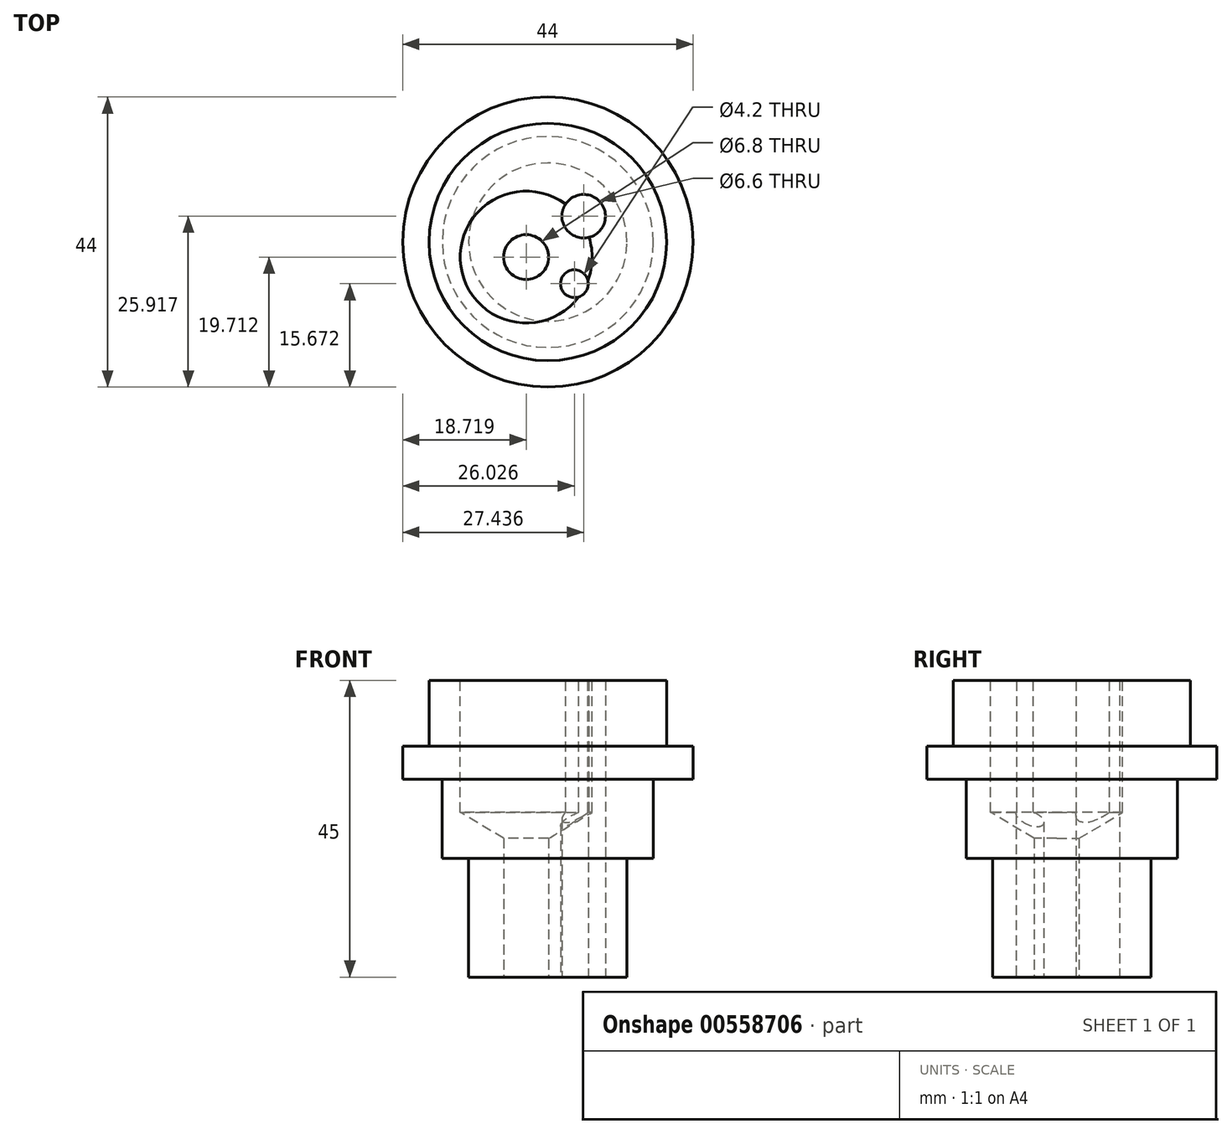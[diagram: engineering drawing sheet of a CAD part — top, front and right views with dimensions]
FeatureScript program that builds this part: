
annotation { "Feature Type Name" : "Feature", "Feature Type Description" : "" }
export const myFeature = defineFeature(function(context is Context, id is Id, definition is map)
    precondition{}
    {
        {
            var Q0;
            Q0=qCreatedBy(makeId("Top.planeOp"),FACE);
            var sketch = newSketch(context, id + "F0", { "sketchPlane" : qUnion([Q0])});
            skCircle(sketch, "E0", {"center": v(0, 0) * mm, "radius": 12 * mm});
            skCircle(sketch, "E1", {"center": v(0, 0) * mm, "radius": 18 * mm});
            skCircle(sketch, "E2", {"center": v(5.44, 3.92) * mm, "radius": 8.25 * mm, "construction": true});
            skCircle(sketch, "E3", {"center": v(5.44, 3.92) * mm, "radius": 3.3 * mm, "construction": true});
            skCircle(sketch, "E4", {"center": v(-3.28, -2.29) * mm, "radius": 4 * mm, "construction": true});
            skCircle(sketch, "E5", {"center": v(-3.28, -2.29) * mm, "radius": 6 * mm, "construction": true});
            skCircle(sketch, "E6", {"center": v(-3.28, -2.29) * mm, "radius": 10 * mm, "construction": true});
            skCircle(sketch, "E7", {"center": v(4.03, -6.33) * mm, "radius": 2.5 * mm});
            skCircle(sketch, "E8", {"center": v(0, 0) * mm, "radius": 17 * mm, "construction": true});
            skCircle(sketch, "E9", {"center": v(0, 0) * mm, "radius": 10 * mm, "construction": true});
            skLineSegment(sketch, "E10", {"start": v(0, 0) * mm, "end": v(-14.77, -10.3) * mm, "construction": true});
            skLineSegment(sketch, "E11", {"start": v(0, 0) * mm, "end": v(14.6, 10.52) * mm, "construction": true});
            skLineSegment(sketch, "E12", {"start": v(0, 0) * mm, "end": v(9.66, -15.19) * mm, "construction": true});
            skPoint(sketch, "E13", {"position": v(-8.2, -5.72) * mm});
            skPoint(sketch, "E14", {"position": v(8.11, 5.85) * mm});
            skPoint(sketch, "E15", {"position": v(5.37, -8.44) * mm});
            skCircle(sketch, "E16", {"center": v(0, 0) * mm, "radius": 16 * mm});
            skCircle(sketch, "E17", {"center": v(0, 0) * mm, "radius": 22 * mm});
            skSolve(sketch);
        }
        {
            var Q0;
            Q0=qCreatedBy(makeId("Right.planeOp"),FACE);
            var sketch = newSketch(context, id + "F1", { "sketchPlane" : qUnion([Q0])});
            skLineSegment(sketch, "E18.0", {"start": v(-22, 0) * mm, "end": v(22, 0) * mm});
            skLineSegment(sketch, "E19.0", {"start": v(-18, 0) * mm, "end": v(18, 0) * mm, "construction": true});
            skLineSegment(sketch, "E20.0", {"start": v(-16, 0) * mm, "end": v(16, 0) * mm, "construction": true});
            skLineSegment(sketch, "E21.0", {"start": v(-12, 0) * mm, "end": v(12, 0) * mm, "construction": true});
            skLineSegment(sketch, "E22", {"start": v(0, 27.72) * mm, "end": v(0, -43.34) * mm, "construction": true});
            skLineSegment(sketch, "E23", {"start": v(-22, 0) * mm, "end": v(-22, 5) * mm});
            skLineSegment(sketch, "E24", {"start": v(-22, 5) * mm, "end": v(-18, 5) * mm});
            skLineSegment(sketch, "E25", {"start": v(-18, 5) * mm, "end": v(-18, 15) * mm});
            skLineSegment(sketch, "E26", {"start": v(-18, 15) * mm, "end": v(0, 15) * mm});
            skLineSegment(sketch, "E27", {"start": v(-16, 0) * mm, "end": v(-16, -12) * mm});
            skLineSegment(sketch, "E28", {"start": v(-16, -12) * mm, "end": v(-12, -12) * mm});
            skLineSegment(sketch, "E29", {"start": v(-12, -12) * mm, "end": v(-12, -30) * mm});
            skLineSegment(sketch, "E30", {"start": v(-12, -30) * mm, "end": v(0, -30) * mm});
            skLineSegment(sketch, "E31", {"start": v(0, 15) * mm, "end": v(0, -30) * mm});
            skSolve(sketch);
        }
        {
            var Q0;
            {var subQ0=sQuery(id+"F1.wireOp",EDGE,"E27");Q0=makeQuery(id+"F1.imprint","IMPRINT",FACE,{"disambiguationData":[TD([[makeQuery(id+"F1.imprint","IMPRINT",EDGE,{"derivedFrom":subQ0}),1.0]])]});}
            var Q1;
            {var subQ0=sQuery(id+"F1.wireOp",EDGE,"E23");Q1=makeQuery(id+"F1.imprint","IMPRINT",FACE,{"disambiguationData":[TD([[makeQuery(id+"F1.imprint","IMPRINT",EDGE,{"derivedFrom":subQ0}),-1.0]])]});}
            var Q2;
            Q2=sQuery(id+"F1.wireOp",EDGE,"E22");
            revolve(context, id + "F2", {"entities" : qUnion([Q0, Q1]), "axis" : qUnion([Q2]), "revolveType" : RevolveType.FULL});
        }
        {
            var Q0;
            Q0=makeQuery(id+"F2.opRevolve","SWEPT_FACE",FACE,{"disambiguationData":[OSD([sQuery(id+"F1.wireOp",EDGE,"E30")])]});
            var sketch = newSketch(context, id + "F3", { "sketchPlane" : qUnion([Q0])});
            skPoint(sketch, "E32.0", {"position": v(4.03, 6.33) * mm});
            skPoint(sketch, "E33.0", {"position": v(-3.28, 2.29) * mm});
            skPoint(sketch, "E34.0", {"position": v(5.44, -3.92) * mm});
            skSolve(sketch);
        }
        {
            var Q0;
            Q0=sQuery(id+"F3.wireOp",VERTEX,"E32.0");
            var Q1;
            Q1=makeQuery(id+"F2.opRevolve","SWEPT_BODY",BODY,{"disambiguationData":[OSD([sQuery(id+"F1.wireOp",EDGE,"E18.0"),sQuery(id+"F1.wireOp",EDGE,"E23"),sQuery(id+"F1.wireOp",EDGE,"E24"),sQuery(id+"F1.wireOp",EDGE,"E25"),sQuery(id+"F1.wireOp",EDGE,"E26"),sQuery(id+"F1.wireOp",EDGE,"E27"),sQuery(id+"F1.wireOp",EDGE,"E28"),sQuery(id+"F1.wireOp",EDGE,"E29"),sQuery(id+"F1.wireOp",EDGE,"E30"),sQuery(id+"F1.wireOp",EDGE,"E31")])]});
            hole(context, id + "F4", {"style" : HoleStyle.SIMPLE, "endStyle" : HoleEndStyle.THROUGH, "standardTappedOrClearance" : lookupTablePath({ "standard" : "ISO", "engagement" : "75%", "pitch" : "0.8 mm", "size" : "M5", "type" : "Tapped" }), "standardBlindInLast" : lookupTablePath({ "standard" : "ISO", "engagement" : "75%", "pitch" : "0.8 mm", "size" : "M5", "type" : "Tapped" }), "holeDiameter" : 4.2 * mm, "majorDiameter" : 5 * mm, "showTappedDepth" : true, "tappedDepth" : 3.6 * mm, "tapClearance" : 3, "locations" : qUnion([Q0]), "scope" : qUnion([Q1])});
        }
        {
            var Q0;
            Q0=sQuery(id+"F3.wireOp",VERTEX,"E33.0");
            var Q1;
            Q1=makeQuery(id+"F2.opRevolve","SWEPT_BODY",BODY,{"disambiguationData":[OSD([sQuery(id+"F1.wireOp",EDGE,"E18.0"),sQuery(id+"F1.wireOp",EDGE,"E23"),sQuery(id+"F1.wireOp",EDGE,"E24"),sQuery(id+"F1.wireOp",EDGE,"E25"),sQuery(id+"F1.wireOp",EDGE,"E26"),sQuery(id+"F1.wireOp",EDGE,"E27"),sQuery(id+"F1.wireOp",EDGE,"E28"),sQuery(id+"F1.wireOp",EDGE,"E29"),sQuery(id+"F1.wireOp",EDGE,"E30"),sQuery(id+"F1.wireOp",EDGE,"E31")])]});
            hole(context, id + "F5", {"style" : HoleStyle.SIMPLE, "endStyle" : HoleEndStyle.THROUGH, "standardTappedOrClearance" : lookupTablePath({ "standard" : "ISO", "engagement" : "75%", "pitch" : "1.25 mm", "size" : "M8", "type" : "Tapped" }), "standardBlindInLast" : lookupTablePath({ "standard" : "ISO", "engagement" : "75%", "pitch" : "1.25 mm", "size" : "M8", "type" : "Tapped" }), "holeDiameter" : 6.8 * mm, "majorDiameter" : 8 * mm, "showTappedDepth" : true, "tappedDepth" : 3.6 * mm, "tapClearance" : 3, "locations" : qUnion([Q0]), "scope" : qUnion([Q1])});
        }
        {
            var Q0;
            Q0=sQuery(id+"F3.wireOp",VERTEX,"E34.0");
            var Q1;
            Q1=makeQuery(id+"F2.opRevolve","SWEPT_BODY",BODY,{"disambiguationData":[OSD([sQuery(id+"F1.wireOp",EDGE,"E18.0"),sQuery(id+"F1.wireOp",EDGE,"E23"),sQuery(id+"F1.wireOp",EDGE,"E24"),sQuery(id+"F1.wireOp",EDGE,"E25"),sQuery(id+"F1.wireOp",EDGE,"E26"),sQuery(id+"F1.wireOp",EDGE,"E27"),sQuery(id+"F1.wireOp",EDGE,"E28"),sQuery(id+"F1.wireOp",EDGE,"E29"),sQuery(id+"F1.wireOp",EDGE,"E30"),sQuery(id+"F1.wireOp",EDGE,"E31")])]});
            hole(context, id + "F6", {"style" : HoleStyle.SIMPLE, "endStyle" : HoleEndStyle.THROUGH, "standardTappedOrClearance" : lookupTablePath({ "standard" : "ISO", "fit" : "Normal", "size" : "M6", "type" : "Clearance" }), "standardBlindInLast" : lookupTablePath({ "fit" : "Standard", "standard" : "ISO", "size" : "M6", "type" : "Clearance" }), "holeDiameter" : 6.6 * mm, "majorDiameter" : 6 * mm, "tappedDepth" : 3.6 * mm, "tapClearance" : 3, "locations" : qUnion([Q0]), "scope" : qUnion([Q1])});
        }
        {
            var Q0;
            Q0=makeQuery(id+"F2.opRevolve","SWEPT_FACE",FACE,{"disambiguationData":[OSD([sQuery(id+"F1.wireOp",EDGE,"E26")])]});
            var sketch = newSketch(context, id + "F7", { "sketchPlane" : qUnion([Q0])});
            skPoint(sketch, "E35.0", {"position": v(-3.28, -2.29) * mm});
            skSolve(sketch);
        }
        {
            var Q0;
            Q0=sQuery(id+"F7.wireOp",VERTEX,"E35.0");
            var Q1;
            Q1=makeQuery(id+"F2.opRevolve","SWEPT_BODY",BODY,{"disambiguationData":[OSD([sQuery(id+"F1.wireOp",EDGE,"E18.0"),sQuery(id+"F1.wireOp",EDGE,"E23"),sQuery(id+"F1.wireOp",EDGE,"E24"),sQuery(id+"F1.wireOp",EDGE,"E25"),sQuery(id+"F1.wireOp",EDGE,"E26"),sQuery(id+"F1.wireOp",EDGE,"E27"),sQuery(id+"F1.wireOp",EDGE,"E28"),sQuery(id+"F1.wireOp",EDGE,"E29"),sQuery(id+"F1.wireOp",EDGE,"E30"),sQuery(id+"F1.wireOp",EDGE,"E31")])]});
            hole(context, id + "F8", {"style" : HoleStyle.SIMPLE, "endStyle" : HoleEndStyle.BLIND, "standardTappedOrClearance" : lookupTablePath({ "standard" : "ISO", "size" : "20", "type" : "Drilled" }), "standardBlindInLast" : lookupTablePath({ "standard" : "ISO", "size" : "20", "type" : "Drilled" }), "holeDiameter" : 20 * mm, "majorDiameter" : 20 * mm, "holeDepth" : 20 * mm, "tappedDepth" : 3.6 * mm, "tapClearance" : 3, "locations" : qUnion([Q0]), "scope" : qUnion([Q1])});
        }
    });
